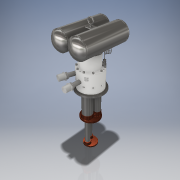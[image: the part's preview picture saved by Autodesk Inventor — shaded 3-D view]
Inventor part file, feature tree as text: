
AUTODESK INVENTOR PART (.ipt)
format: ipt  version: 2018 (Build 220112000, 112)  size: 2,975,744 bytes
history: native  units: in
note: dims shown in document units (in); Inventor stores cm internally (conversion verified against a paired STEP export)
features: extrude x1, sketch x1
ambient origin geometry x8: Origin, YZ Plane, XZ Plane, XY Plane, X Axis, Y Axis, Z Axis, Center Point
bodies: Solid2 (feature_tree), Solid1 (feature_tree)
feature tree (2):
  extrude  "Extrusion1"  [1 undecoded]
  sketch  "Sketch1"  dims[d0=3.6875in d1=0.0in]
note: 1 required parameter value undecoded (feature->parameter linkage not recoverable at this tier; creation-order binding heuristic only, values carry confidence <= 0.55)
